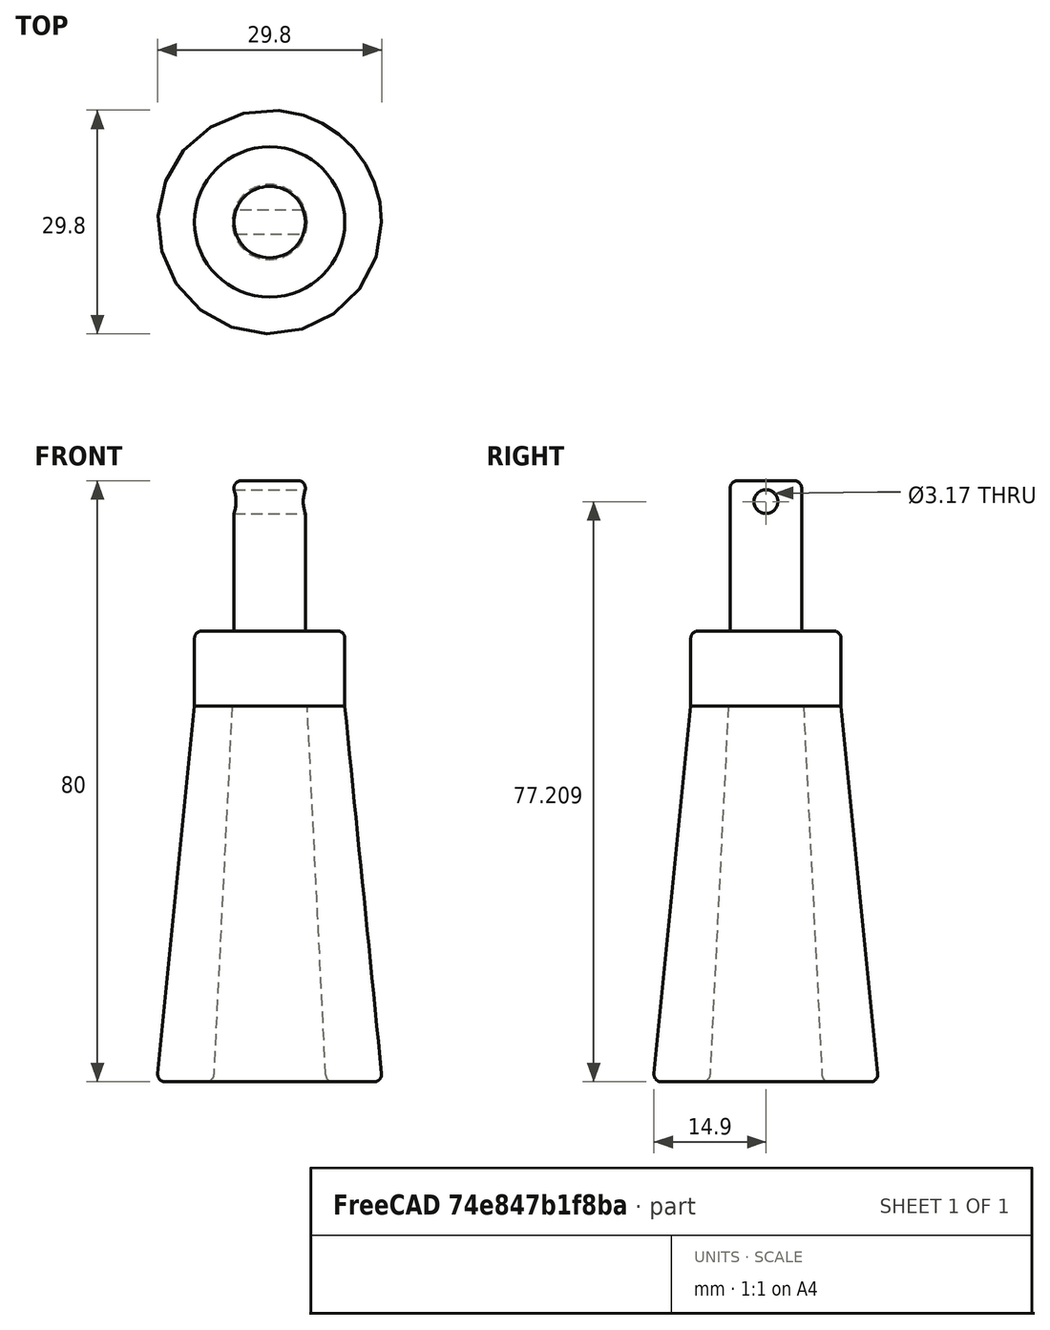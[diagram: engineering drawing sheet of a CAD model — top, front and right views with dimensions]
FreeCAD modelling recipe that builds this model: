
FCSTD DOCUMENT  (FreeCAD 0.19R24291 (Git))
Label: WorkBenchHandle
License: All rights reserved
LicenseURL: http://en.wikipedia.org/wiki/All_rights_reserved
objects: TechDraw::DrawViewDimension×9, Sketcher::SketchObject×5, PartDesign::Fillet×4, TechDraw::DrawProjGroupItem×4, PartDesign::Pad×2, PartDesign::AdditiveLoft×1, PartDesign::Pocket×1, TechDraw::DrawSVGTemplate×1, PartDesign::Body×1, TechDraw::DrawProjGroup×1, TechDraw::DrawPage×1
note: 22 computed .brp shape members not serialized (recipe doc carries the construction recipe); baked Part::Feature solids carry a one-line shape summary decoded from their .brp

FEATURE [Sketcher::SketchObject] Sketch
  FullyConstrained = true
  MapMode = 5
  Support = -> [XY_Plane]
  sketch-geometry (2):
    g0: Circle CenterX=0 CenterY=0 CenterZ=0 NormalX=0 NormalY=0 NormalZ=1 AngleXU=0 Radius=15
    g1: Circle CenterX=0 CenterY=0 CenterZ=0 NormalX=0 NormalY=0 NormalZ=1 AngleXU=0 Radius=7.5
  constraints (4):
    c: Coincident(g0,g-1)
    c: Coincident(g1,g0)
    c: Diameter(g0) = 30
    c: Diameter(g1) = 15
FEATURE [Sketcher::SketchObject] Sketch001
  AttachmentOffset = pos=(0,0,50) rot=(0,0,1;0rad)
  FullyConstrained = true
  MapMode = 5
  Placement = pos=(0,0,50) rot=(0,0,1;0rad)
  Support = -> [XY_Plane]
  sketch-geometry (2):
    g0: Circle CenterX=0 CenterY=0 CenterZ=0 NormalX=0 NormalY=0 NormalZ=1 AngleXU=0 Radius=10
    g1: Circle CenterX=0 CenterY=0 CenterZ=0 NormalX=0 NormalY=0 NormalZ=1 AngleXU=0 Radius=5
  constraints (4):
    c: Coincident(g0,g-1)
    c: Coincident(g1,g0)
    c: Diameter(g0) = 20
    c: Diameter(g1) = 10
FEATURE [PartDesign::AdditiveLoft] AdditiveLoft  label="AdditiveLoftHandel"
  Closed = false
  Profile = -> Sketch
  Ruled = false
  Sections = -> [Sketch001]
FEATURE [Sketcher::SketchObject] Sketch002
  FullyConstrained = true
  MapMode = 5
  Placement = pos=(0,0,50) rot=(0,0,1;0rad)
  Support = -> [AdditiveLoft]
  sketch-geometry (1):
    g0: Circle CenterX=0 CenterY=0 CenterZ=0 NormalX=0 NormalY=0 NormalZ=1 AngleXU=0 Radius=10
  constraints (2):
    c: Coincident(g0,g-1)
    c: Diameter(g0) = 20
FEATURE [PartDesign::Pad] Pad  label="PadBoss"
  BaseFeature = -> AdditiveLoft
  Direction = (1,1,1)
  Length = 10
  Length2 = 100
  Profile = -> Sketch002
  Type = 0
FEATURE [Sketcher::SketchObject] Sketch003
  FullyConstrained = true
  MapMode = 5
  Placement = pos=(0,0,60) rot=(0,0,1;0rad)
  Support = -> [Pad]
  sketch-geometry (1):
    g0: Circle CenterX=0 CenterY=0 CenterZ=0 NormalX=0 NormalY=0 NormalZ=1 AngleXU=0 Radius=4.75
  constraints (2):
    c: Coincident(g0,g-1)
    c: Diameter(g0) = 9.5
FEATURE [PartDesign::Pad] Pad001  label="PadPin"
  BaseFeature = -> Pad
  Direction = (1,1,1)
  Length = 20
  Length2 = 100
  Profile = -> Sketch003
  Type = 0
FEATURE [Sketcher::SketchObject] Sketch004
  FullyConstrained = false
  MapMode = 5
  Placement = pos=(0,0,0) rot=(0.57735,0.57735,0.57735;2.0944rad)
  Support = -> [YZ_Plane]
  sketch-geometry (1):
    g0: Circle CenterX=0 CenterY=77.2086 CenterZ=0 NormalX=0 NormalY=0 NormalZ=1 AngleXU=0 Radius=1.5875
  constraints (2):
    c: PointOnObject(g0,g-2)
    c: Diameter(g0) = 3.175
FEATURE [PartDesign::Pocket] Pocket
  BaseFeature = -> Pad001
  Length = 5
  Length2 = 100
  Midplane = true
  Profile = -> Sketch004
  Reversed = true
  Type = 1
FEATURE [TechDraw::DrawSVGTemplate] Template
  EditableTexts = Approved1=Approved 1; Approved2=Approved 2; CheckedBy=on 20230706; Code=Code; CompanyAddress=3433 Riegeway Trail; CompanyName=Amused Scientist; DrawingNumber=Drawing Number; DrawingTitle1=WorkBenchHandle; DrawingTitle2=Drawing Title 2; DrawingTitle3=Drawing Title 3; DrawnBy=Lee Erickson; Revision=Rev; Scale=Scale 1:1; Sheet=Sheet n of m
  Height = 215.9
  Orientation = 1
  Width = 279.4
FEATURE [PartDesign::Fillet] Fillet
  Base = -> Pocket [Edge13]
  BaseFeature = -> Pocket
  Radius = 1
  SupportTransform = false
FEATURE [PartDesign::Fillet] Fillet001
  Base = -> Fillet [Edge12]
  BaseFeature = -> Fillet
  Radius = 1
  SupportTransform = false
FEATURE [PartDesign::Fillet] Fillet002
  Base = -> Fillet001 [Edge17]
  BaseFeature = -> Fillet001
  Radius = 1
  SupportTransform = false
FEATURE [PartDesign::Fillet] Fillet003
  Base = -> Fillet002 [Edge8]
  BaseFeature = -> Fillet002
  Radius = 1
  SupportTransform = false
FEATURE [PartDesign::Body] Body
  Group = -> [Sketch,Sketch001,AdditiveLoft,Sketch002,Pad,Sketch003,Pad001,Sketch004,Pocket,Fillet,Fillet001,Fillet002,Fillet003]
  Origin = -> Origin
  Tip = -> Fillet003
FEATURE [TechDraw::DrawProjGroupItem] ProjItem004  label="Front001"
  CoarseView = false
  Direction = (1,0,0)
  Focus = 100
  HardHidden = false
  IsoCount = 0
  IsoHidden = false
  IsoVisible = false
  LockPosition = true
  Perspective = false
  Rotation = 0
  RotationVector = (0,0,1)
  ScaleType = 2
  SeamHidden = false
  SeamVisible = false
  SmoothHidden = false
  SmoothVisible = false
  Source = -> [Body]
  Type = 0
  X = 0
  XDirection = (0,0,1)
  Y = 0
FEATURE [TechDraw::DrawProjGroupItem] ProjItem005  label="FrontBottomLeft001"
  CoarseView = false
  Direction = (0.57735,0.57735,-0.57735)
  Focus = 100
  HardHidden = false
  IsoCount = 0
  IsoHidden = false
  IsoVisible = false
  LockPosition = true
  Perspective = false
  Rotation = 0
  RotationVector = (1,0,0)
  ScaleType = 2
  SeamHidden = false
  SeamVisible = false
  SmoothHidden = false
  SmoothVisible = false
  Source = -> [Body]
  Type = 8
  X = 90.1975
  XDirection = (0.707107,0,0.707107)
  Y = 67.4708
FEATURE [TechDraw::DrawProjGroupItem] ProjItem006  label="Right001"
  CoarseView = false
  Direction = (1e-16,0,1)
  Focus = 100
  HardHidden = false
  IsoCount = 0
  IsoHidden = false
  IsoVisible = false
  LockPosition = true
  Perspective = false
  Rotation = 0
  RotationVector = (1,0,0)
  ScaleType = 2
  SeamHidden = false
  SeamVisible = false
  SmoothHidden = false
  SmoothVisible = false
  Source = -> [Body]
  Type = 2
  X = -69.895
  XDirection = (-1,0,1e-16)
  Y = 0
FEATURE [TechDraw::DrawProjGroupItem] ProjItem007  label="FrontBottomRight001"
  CoarseView = false
  Direction = (0.57735,0.57735,0.57735)
  Focus = 100
  HardHidden = false
  IsoCount = 0
  IsoHidden = false
  IsoVisible = false
  LockPosition = true
  Perspective = false
  Rotation = 0
  RotationVector = (1,0,0)
  ScaleType = 2
  SeamHidden = false
  SeamVisible = false
  SmoothHidden = false
  SmoothVisible = false
  Source = -> [Body]
  Type = 9
  X = -5.79715
  XDirection = (-0.707107,0,0.707107)
  Y = 61.3243
FEATURE [TechDraw::DrawProjGroup] ProjGroup001  label="ProjGroup"
  Anchor = -> ProjItem004
  AutoDistribute = true
  LockPosition = false
  ProjectionType = 0
  Rotation = 0
  ScaleType = 0
  Source = -> [Body]
  Views = -> [ProjItem004,ProjItem005,ProjItem006,ProjItem007]
  X = 120.351
  Y = 96.2835
  spacingX = 15
  spacingY = 15
FEATURE [TechDraw::DrawViewDimension] Dimension010
  Arbitrary = false
  ArbitraryTolerances = false
  EqualTolerance = true
  FormatSpec = %.2f
  FormatSpecOverTolerance = %+.2f
  FormatSpecUnderTolerance = %+.2f
  Inverted = false
  LockPosition = false
  MeasureType = 1
  OverTolerance = 0
  References2D = -> [ProjItem004]
  Rotation = 0
  ScaleType = 0
  TheoreticalExact = false
  Type = 1
  UnderTolerance = 0
  X = 50.3096
  Y = 17.2342
FEATURE [TechDraw::DrawViewDimension] Dimension011
  Arbitrary = false
  ArbitraryTolerances = false
  EqualTolerance = true
  FormatSpec = %.2f
  FormatSpecOverTolerance = %+.2f
  FormatSpecUnderTolerance = %+.2f
  Inverted = false
  LockPosition = false
  MeasureType = 1
  OverTolerance = 0
  References2D = -> [ProjItem004]
  Rotation = 0
  ScaleType = 0
  TheoreticalExact = false
  Type = 2
  UnderTolerance = 0
  X = 96.2885
  Y = 6.82798
FEATURE [TechDraw::DrawViewDimension] Dimension012
  Arbitrary = false
  ArbitraryTolerances = false
  EqualTolerance = true
  FormatSpec = %.2f
  FormatSpecOverTolerance = %+.2f
  FormatSpecUnderTolerance = %+.2f
  Inverted = false
  LockPosition = false
  MeasureType = 1
  OverTolerance = 0
  References2D = -> [ProjItem004]
  Rotation = 0
  ScaleType = 0
  TheoreticalExact = false
  Type = 2
  UnderTolerance = 0
  X = 81.4148
  Y = 22.363
FEATURE [TechDraw::DrawViewDimension] Dimension013
  Arbitrary = false
  ArbitraryTolerances = false
  EqualTolerance = true
  FormatSpec = %.2f
  FormatSpecOverTolerance = %+.2f
  FormatSpecUnderTolerance = %+.2f
  Inverted = false
  LockPosition = false
  MeasureType = 1
  OverTolerance = 0
  References2D = -> [ProjItem004]
  Rotation = 0
  ScaleType = 0
  TheoreticalExact = false
  Type = 1
  UnderTolerance = 0
  X = 25.6521
  Y = -14.7617
FEATURE [TechDraw::DrawViewDimension] Dimension014
  Arbitrary = false
  ArbitraryTolerances = false
  EqualTolerance = true
  FormatSpec = %.2f
  FormatSpecOverTolerance = %+.2f
  FormatSpecUnderTolerance = %+.2f
  Inverted = false
  LockPosition = false
  MeasureType = 1
  OverTolerance = 0
  References2D = -> [ProjItem004]
  Rotation = 0
  ScaleType = 0
  TheoreticalExact = false
  Type = 1
  UnderTolerance = 0
  X = 24.4376
  Y = 21.2028
FEATURE [TechDraw::DrawViewDimension] Dimension015
  Arbitrary = false
  ArbitraryTolerances = false
  EqualTolerance = true
  FormatSpec = %.2f
  FormatSpecOverTolerance = %+.2f
  FormatSpecUnderTolerance = %+.2f
  Inverted = false
  LockPosition = false
  MeasureType = 1
  OverTolerance = 0
  References2D = -> [ProjItem004]
  Rotation = 0
  ScaleType = 0
  TheoreticalExact = false
  Type = 1
  UnderTolerance = 0
  X = -16.3725
  Y = 25.6721
FEATURE [TechDraw::DrawViewDimension] Dimension016
  Arbitrary = false
  ArbitraryTolerances = false
  EqualTolerance = true
  FormatSpec = %.2f
  FormatSpecOverTolerance = %+.2f
  FormatSpecUnderTolerance = %+.2f
  Inverted = false
  LockPosition = false
  MeasureType = 1
  OverTolerance = 0
  References2D = -> [ProjItem004]
  Rotation = 0
  ScaleType = 0
  TheoreticalExact = false
  Type = 1
  UnderTolerance = 0
  X = 16.6174
  Y = 29.4666
FEATURE [TechDraw::DrawViewDimension] Dimension017
  Arbitrary = false
  ArbitraryTolerances = false
  EqualTolerance = true
  FormatSpec = %.2f
  FormatSpecOverTolerance = %+.2f
  FormatSpecUnderTolerance = %+.2f
  Inverted = false
  LockPosition = false
  MeasureType = 1
  OverTolerance = 0
  References2D = -> [ProjItem004]
  Rotation = 0
  ScaleType = 0
  TheoreticalExact = false
  Type = 2
  UnderTolerance = 0
  X = -53.2163
  Y = 2.02701
FEATURE [TechDraw::DrawViewDimension] Dimension018
  Arbitrary = false
  ArbitraryTolerances = false
  EqualTolerance = true
  FormatSpec = ⌀%.2f
  FormatSpecOverTolerance = %+.2f
  FormatSpecUnderTolerance = %+.2f
  Inverted = false
  LockPosition = false
  MeasureType = 1
  OverTolerance = 0
  References2D = -> [ProjItem004]
  Rotation = 0
  ScaleType = 0
  TheoreticalExact = false
  Type = 5
  UnderTolerance = 0
  X = 62.6584
  Y = -16.9741
FEATURE [TechDraw::DrawPage] Page  label="PageHandel"
  KeepUpdated = true
  NextBalloonIndex = 1
  ProjectionType = 0
  Template = -> Template
  Views = -> [ProjGroup001,Dimension010,Dimension011,Dimension012,Dimension013,Dimension014,Dimension015,Dimension016,Dimension017,Dimension018]
